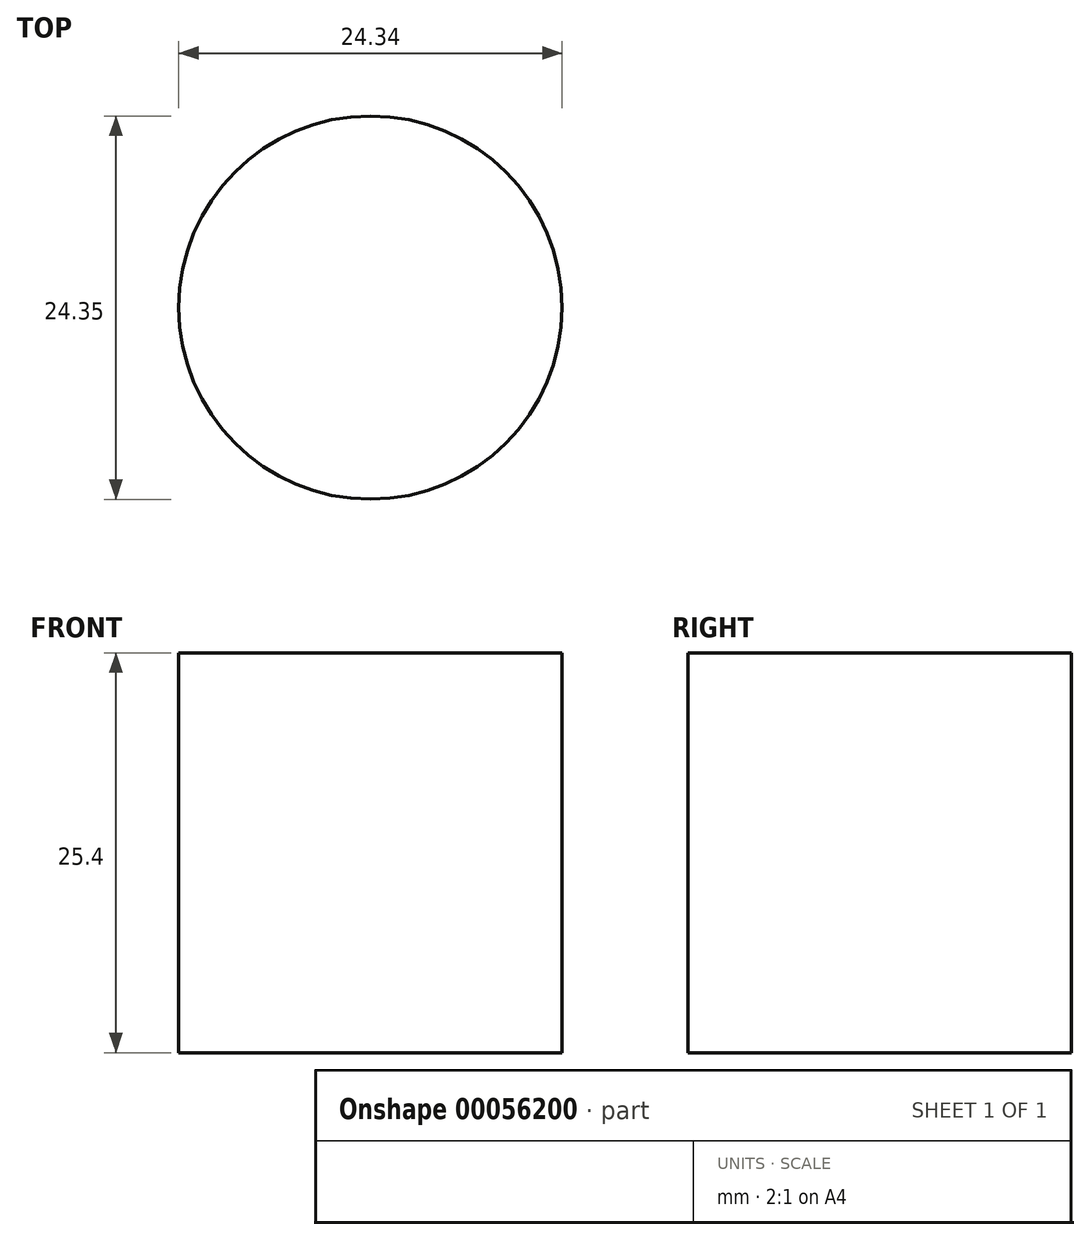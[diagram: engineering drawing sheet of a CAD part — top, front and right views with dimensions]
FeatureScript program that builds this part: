
annotation { "Feature Type Name" : "Feature", "Feature Type Description" : "" }
export const myFeature = defineFeature(function(context is Context, id is Id, definition is map)
    precondition{}
    {
        {
            var Q0;
            Q0=qCreatedBy(makeId("Top.planeOp"),FACE);
            var sketch = newSketch(context, id + "F0", { "sketchPlane" : qUnion([Q0])});
            skCircle(sketch, "E0", {"center": v(-61.65, -50.48) * mm, "radius": 12.17 * mm});
            skSolve(sketch);
        }
        {
            var Q0;
            Q0=makeQuery(id+"F0.imprint","IMPRINT",FACE,{"disambiguationData":[TD([[makeQuery(id+"F0.imprint","IMPRINT",EDGE,{"derivedFrom":sQuery(id+"F0.wireOp",EDGE,"E0")}),1.0]])]});
            extrude(context, id + "F1", {"entities" : qUnion([Q0]), "oppositeDirection" : true, "depth" : 25.4 * mm});
        }
    });
